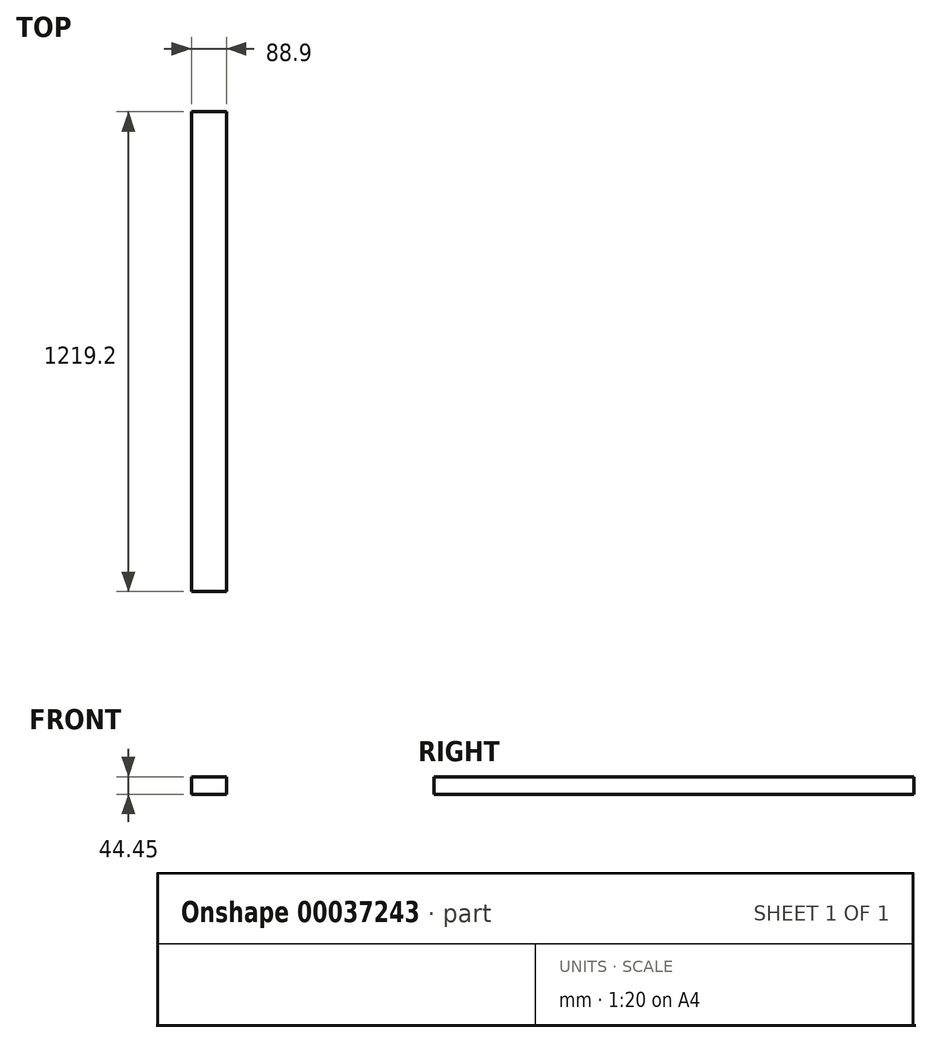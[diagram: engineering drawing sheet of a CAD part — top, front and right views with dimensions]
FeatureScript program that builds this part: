
annotation { "Feature Type Name" : "Feature", "Feature Type Description" : "" }
export const myFeature = defineFeature(function(context is Context, id is Id, definition is map)
    precondition{}
    {
        {
            var Q0;
            Q0=qCreatedBy(makeId("Front.planeOp"),FACE);
            var sketch = newSketch(context, id + "F0", { "sketchPlane" : qUnion([Q0])});
            skLineSegment(sketch, "E0.bottom", {"start": v(0, 0) * mm, "end": v(88.9, 0) * mm});
            skLineSegment(sketch, "E0.top", {"start": v(0, 44.45) * mm, "end": v(88.9, 44.45) * mm});
            skLineSegment(sketch, "E0.left", {"start": v(0, 0) * mm, "end": v(0, 44.45) * mm});
            skLineSegment(sketch, "E0.right", {"start": v(88.9, 0) * mm, "end": v(88.9, 44.45) * mm});
            skSolve(sketch);
        }
        {
            var Q0;
            Q0=makeQuery(id+"F0.imprint","IMPRINT",FACE,{"disambiguationData":[TD([[makeQuery(id+"F0.imprint","IMPRINT",EDGE,{"derivedFrom":sQuery(id+"F0.wireOp",EDGE,"E0.bottom")}),1.0]])]});
            extrude(context, id + "F1", {"entities" : qUnion([Q0]), "depth" : 1219.2 * mm});
        }
    });
